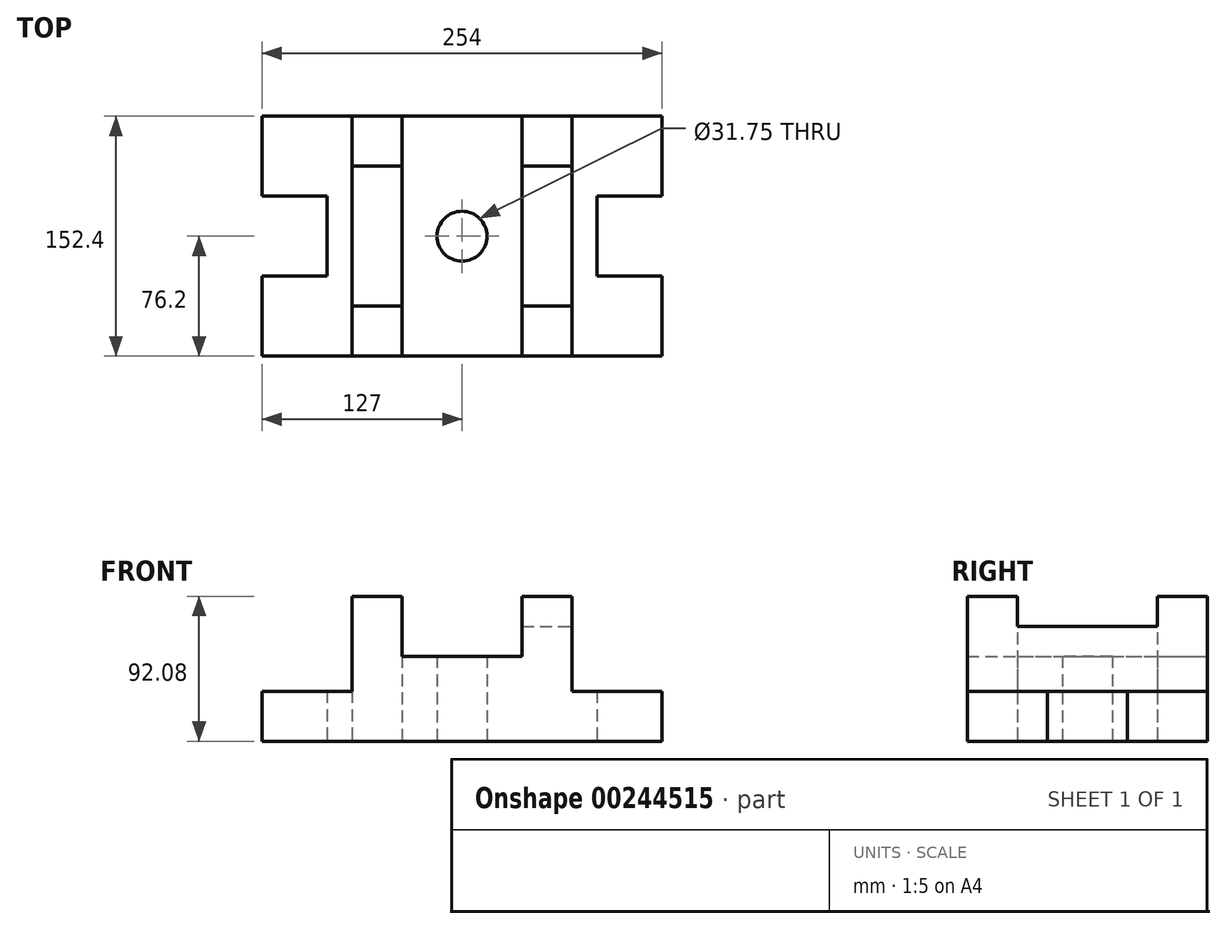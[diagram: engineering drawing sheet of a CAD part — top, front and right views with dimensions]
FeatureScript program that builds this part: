
annotation { "Feature Type Name" : "Feature", "Feature Type Description" : "" }
export const myFeature = defineFeature(function(context is Context, id is Id, definition is map)
    precondition{}
    {
        {
            var Q0;
            Q0=qCreatedBy(makeId("Top.planeOp"),FACE);
            var sketch = newSketch(context, id + "F0", { "sketchPlane" : qUnion([Q0])});
            skCircle(sketch, "E0", {"center": v(0, 0) * mm, "radius": 15.88 * mm});
            skLineSegment(sketch, "E1.bottom", {"start": v(38.1, -76.2) * mm, "end": v(-38.1, -76.2) * mm});
            skLineSegment(sketch, "E1.top", {"start": v(38.1, 76.2) * mm, "end": v(-38.1, 76.2) * mm});
            skLineSegment(sketch, "E1.left", {"start": v(38.1, -76.2) * mm, "end": v(38.1, 76.2) * mm});
            skLineSegment(sketch, "E1.right", {"start": v(-38.1, -76.2) * mm, "end": v(-38.1, 76.2) * mm});
            skLineSegment(sketch, "E2.bottom", {"start": v(-38.1, -76.2) * mm, "end": v(-69.85, -76.2) * mm});
            skLineSegment(sketch, "E2.top", {"start": v(-38.1, -44.45) * mm, "end": v(-69.85, -44.45) * mm});
            skLineSegment(sketch, "E2.left", {"start": v(-38.1, -76.2) * mm, "end": v(-38.1, -44.45) * mm});
            skLineSegment(sketch, "E2.right", {"start": v(-69.85, -76.2) * mm, "end": v(-69.85, -44.45) * mm});
            skLineSegment(sketch, "E3.bottom", {"start": v(38.1, -76.2) * mm, "end": v(69.85, -76.2) * mm});
            skLineSegment(sketch, "E3.top", {"start": v(38.1, -44.45) * mm, "end": v(69.85, -44.45) * mm});
            skLineSegment(sketch, "E3.left", {"start": v(38.1, -76.2) * mm, "end": v(38.1, -44.45) * mm});
            skLineSegment(sketch, "E3.right", {"start": v(69.85, -76.2) * mm, "end": v(69.85, -44.45) * mm});
            skLineSegment(sketch, "E4.bottom", {"start": v(-38.1, 76.2) * mm, "end": v(-69.85, 76.2) * mm});
            skLineSegment(sketch, "E4.top", {"start": v(-38.1, 44.45) * mm, "end": v(-69.85, 44.45) * mm});
            skLineSegment(sketch, "E4.left", {"start": v(-38.1, 76.2) * mm, "end": v(-38.1, 44.45) * mm});
            skLineSegment(sketch, "E4.right", {"start": v(-69.85, 76.2) * mm, "end": v(-69.85, 44.45) * mm});
            skLineSegment(sketch, "E5.bottom", {"start": v(38.1, 76.2) * mm, "end": v(69.85, 76.2) * mm});
            skLineSegment(sketch, "E5.top", {"start": v(38.1, 44.45) * mm, "end": v(69.85, 44.45) * mm});
            skLineSegment(sketch, "E5.left", {"start": v(38.1, 76.2) * mm, "end": v(38.1, 44.45) * mm});
            skLineSegment(sketch, "E5.right", {"start": v(69.85, 76.2) * mm, "end": v(69.85, 44.45) * mm});
            skLineSegment(sketch, "E6.bottom", {"start": v(-69.85, 44.45) * mm, "end": v(-38.1, 44.45) * mm});
            skLineSegment(sketch, "E6.top", {"start": v(-69.85, -44.45) * mm, "end": v(-38.1, -44.45) * mm});
            skLineSegment(sketch, "E6.left", {"start": v(-69.85, 44.45) * mm, "end": v(-69.85, -44.45) * mm});
            skLineSegment(sketch, "E6.right", {"start": v(-38.1, 44.45) * mm, "end": v(-38.1, -44.45) * mm});
            skLineSegment(sketch, "E7.left", {"start": v(38.1, 44.45) * mm, "end": v(38.1, -44.45) * mm});
            skLineSegment(sketch, "E7.right", {"start": v(69.85, 44.45) * mm, "end": v(69.85, -44.45) * mm});
            skLineSegment(sketch, "E8", {"start": v(69.85, 76.2) * mm, "end": v(127, 76.2) * mm});
            skLineSegment(sketch, "E9", {"start": v(127, 76.2) * mm, "end": v(127, 25.4) * mm});
            skLineSegment(sketch, "E10", {"start": v(127, 25.4) * mm, "end": v(85.72, 25.4) * mm});
            skLineSegment(sketch, "E11", {"start": v(85.72, 25.4) * mm, "end": v(85.72, -25.4) * mm});
            skLineSegment(sketch, "E12", {"start": v(85.72, -25.4) * mm, "end": v(127, -25.4) * mm});
            skLineSegment(sketch, "E13", {"start": v(127, -25.4) * mm, "end": v(127, -76.2) * mm});
            skLineSegment(sketch, "E14", {"start": v(127, -76.2) * mm, "end": v(69.85, -76.2) * mm});
            skLineSegment(sketch, "E15", {"start": v(-69.85, 76.2) * mm, "end": v(-127, 76.2) * mm});
            skLineSegment(sketch, "E16", {"start": v(-127, 76.2) * mm, "end": v(-127, 25.4) * mm});
            skLineSegment(sketch, "E17", {"start": v(-127, 25.4) * mm, "end": v(-85.73, 25.4) * mm});
            skLineSegment(sketch, "E18", {"start": v(-85.73, 25.4) * mm, "end": v(-85.73, -25.4) * mm});
            skLineSegment(sketch, "E19", {"start": v(-85.73, -25.4) * mm, "end": v(-127, -25.4) * mm});
            skLineSegment(sketch, "E20", {"start": v(-127, -25.4) * mm, "end": v(-127, -76.2) * mm});
            skLineSegment(sketch, "E21", {"start": v(-127, -76.2) * mm, "end": v(-69.85, -76.2) * mm});
            skSolve(sketch);
        }
        {
            var Q0;
            Q0 = qSketchRegion(id + "F0", true);
            var Q1;
            Q1=makeQuery(id+"F0.imprint","IMPRINT",FACE,{"disambiguationData":[TD([[makeQuery(id+"F0.imprint","IMPRINT",EDGE,{"derivedFrom":sQuery(id+"F0.wireOp",EDGE,"E6.bottom")}),-1.0]])]});
            var Q2;
            Q2=makeQuery(id+"F0.imprint","IMPRINT",FACE,{"disambiguationData":[TD([[makeQuery(id+"F0.imprint","IMPRINT",EDGE,{"derivedFrom":sQuery(id+"F0.wireOp",EDGE,"E5.top")}),-1.0]])]});
            extrude(context, id + "F1", {"entities" : qUnion([Q0, Q1, Q2]), "depth" : 31.75 * mm});
        }
        {
            var Q0;
            Q0=makeQuery(id+"F0.imprint","IMPRINT",FACE,{"disambiguationData":[TD([[makeQuery(id+"F0.imprint","IMPRINT",EDGE,{"derivedFrom":sQuery(id+"F0.wireOp",EDGE,"E4.bottom")}),1.0]])]});
            var Q1;
            Q1=makeQuery(id+"F0.imprint","IMPRINT",FACE,{"disambiguationData":[TD([[makeQuery(id+"F0.imprint","IMPRINT",EDGE,{"derivedFrom":sQuery(id+"F0.wireOp",EDGE,"E2.bottom")}),-1.0]])]});
            var Q2;
            Q2=makeQuery(id+"F0.imprint","IMPRINT",FACE,{"disambiguationData":[TD([[makeQuery(id+"F0.imprint","IMPRINT",EDGE,{"derivedFrom":sQuery(id+"F0.wireOp",EDGE,"E3.bottom")}),1.0]])]});
            var Q3;
            Q3=makeQuery(id+"F0.imprint","IMPRINT",FACE,{"disambiguationData":[TD([[makeQuery(id+"F0.imprint","IMPRINT",EDGE,{"derivedFrom":sQuery(id+"F0.wireOp",EDGE,"E5.bottom")}),-1.0]])]});
            extrude(context, id + "F2", {"entities" : qUnion([Q0, Q1, Q2, Q3]), "operationType" : NewBodyOperationType.ADD, "depth" : 92.07 * mm});
        }
        {
            var Q0;
            Q0=makeQuery(id+"F0.imprint","IMPRINT",FACE,{"disambiguationData":[TD([[makeQuery(id+"F0.imprint","IMPRINT",EDGE,{"derivedFrom":sQuery(id+"F0.wireOp",EDGE,"E0")}),-1.0]])]});
            extrude(context, id + "F3", {"entities" : qUnion([Q0]), "operationType" : NewBodyOperationType.ADD, "depth" : 53.97 * mm});
        }
        {
            var Q0;
            Q0=makeQuery(id+"F0.imprint","IMPRINT",FACE,{"disambiguationData":[TD([[makeQuery(id+"F0.imprint","IMPRINT",EDGE,{"derivedFrom":sQuery(id+"F0.wireOp",EDGE,"E6.bottom")}),-1.0]])]});
            var Q1;
            Q1=makeQuery(id+"F0.imprint","IMPRINT",FACE,{"disambiguationData":[TD([[makeQuery(id+"F0.imprint","IMPRINT",EDGE,{"derivedFrom":sQuery(id+"F0.wireOp",EDGE,"E5.top")}),-1.0]])]});
            extrude(context, id + "F4", {"entities" : qUnion([Q0, Q1]), "operationType" : NewBodyOperationType.ADD, "depth" : 73.02 * mm});
        }
    });
